# Revit family: E_Cable Tray Support_MEPcontent_OBO Bettermann_Bracket AW FT
name_source: partatom
category: Cable Tray Fittings
revit_build: Autodesk Revit MEP 2015 (Build: 20140606_1530(x64)
units: mm (PartAtom-declared; Revit-internal decimal feet)

## types (34) — shared parameters
Article Description = Wall Bracket
Description = Wall Bracket
EMCS Version = 2.0
ETIM Article Class = EC000022
Family Version = 10.14
Gray = Color RGB 189-187-185
IFCExportAs = IfcCableCarrierFittingType
IFCExportType = NOTDEFINED
MEPcontent Class = CABLE_TRAY_SUPPORT
Manufacturer = OBO BETTERMANN
Manufacturer URL = http://catalog4.obo-bettermann.com
Product Line = OBO BETTERMANN CableTrays
Revit Version = 2015
URL = www.stabiplan.com

## per-type parameters (varying)
| type | Depth | Front Height | GTIN | Height | Height 1 | Manufacturer Art. No. | Width | Width 1 |
| AW 15 11 FT | 40 mm  [stored 0.131234 ft] | 12.5 mm  [stored 0.0410105 ft] | 4012196207077 | 50 mm | 50 mm  [stored 0.164042 ft] | 6420656 | 110 mm | 110 mm  [stored 0.360892 ft] |
| AW 15 16 FT | 40 mm  [stored 0.131234 ft] | 13.75 mm  [stored 0.0451115 ft] | 4012196207138 | 55 mm | 55 mm  [stored 0.180446 ft] | 6420664 | 160 mm | 160 mm  [stored 0.524934 ft] |
| AW 15 21 FT | 40 mm  [stored 0.131234 ft] | 15 mm  [stored 0.0492126 ft] | 4012196207190 | 60 mm | 60 mm  [stored 0.19685 ft] | 6420680 | 210 mm | 210 mm  [stored 0.688976 ft] |
| AW 15 31 FT | 40 mm  [stored 0.131234 ft] | 16.25 mm  [stored 0.0533136 ft] | 4012196207251 | 65 mm | 65 mm  [stored 0.213255 ft] | 6420710 | 310 mm | 310 mm  [stored 1.01706 ft] |
| AW 15 41 FT | 40 mm  [stored 0.131234 ft] | 17.5 mm  [stored 0.0574147 ft] | 4012196207312 | 70 mm | 70 mm  [stored 0.229659 ft] | 6420745 | 410 mm | 410 mm |
| AW 15 51 FT | 40 mm  [stored 0.131234 ft] | 18.75 mm | 4012196207374 | 75 mm | 75 mm | 6420788 | 510 mm | 510 mm |
| AW 15 56 FT | 40 mm  [stored 0.131234 ft] | 20 mm  [stored 0.0656168 ft] | 4012196207435 | 80 mm | 80 mm  [stored 0.262467 ft] | 6420796 | 560 mm | 560 mm |
| AW 15 61 FT | 40 mm  [stored 0.131234 ft] | 20 mm  [stored 0.0656168 ft] | 4012196207497 | 80 mm | 80 mm  [stored 0.262467 ft] | 6420826 | 610 mm | 610 mm |
| AW 30 11 FT | 50 mm  [stored 0.164042 ft] | 15 mm  [stored 0.0492126 ft] | 4012196206599 | 60 mm | 60 mm  [stored 0.19685 ft] | 6419704 | 110 mm | 110 mm  [stored 0.360892 ft] |
| AW 30 16 FT | 50 mm  [stored 0.164042 ft] | 16.25 mm  [stored 0.0533136 ft] | 4012196206650 | 65 mm | 65 mm  [stored 0.213255 ft] | 6419712 | 160 mm | 160 mm  [stored 0.524934 ft] |
| AW 30 21 FT | 50 mm  [stored 0.164042 ft] | 17.5 mm  [stored 0.0574147 ft] | 4012196206711 | 70 mm | 70 mm  [stored 0.229659 ft] | 6419720 | 210 mm | 210 mm  [stored 0.688976 ft] |
| AW 30 31 FT | 50 mm  [stored 0.164042 ft] | 20 mm  [stored 0.0656168 ft] | 4012196206773 | 80 mm | 80 mm  [stored 0.262467 ft] | 6419747 | 310 mm | 310 mm  [stored 1.01706 ft] |
| AW 30 41 FT | 50 mm  [stored 0.164042 ft] | 20 mm  [stored 0.0656168 ft] | 4012196206834 | 80 mm | 80 mm  [stored 0.262467 ft] | 6419763 | 410 mm | 410 mm |
| AW 30 51 FT | 50 mm  [stored 0.164042 ft] | 22.5 mm  [stored 0.0738189 ft] | 4012196206896 | 90 mm | 90 mm  [stored 0.295276 ft] | 6419798 | 510 mm | 510 mm |
| AW 30 56 FT | 50 mm  [stored 0.164042 ft] | 25 mm  [stored 0.082021 ft] | 4012196207015 | 100 mm | 100 mm  [stored 0.328084 ft] | 6419844 | 560 mm | 560 mm |
| AW 30 61 FT | 50 mm  [stored 0.164042 ft] | 25 mm  [stored 0.082021 ft] | 4012196206957 | 100 mm | 100 mm  [stored 0.328084 ft] | 6419828 | 610 mm | 610 mm |
| AW 30 71 FT | 50 mm  [stored 0.164042 ft] | 25 mm  [stored 0.082021 ft] | 4012196483730 | 100 mm | 100 mm  [stored 0.328084 ft] | 6419836 | 710 mm | 710 mm |
| AW 55 21 FT | 50 mm  [stored 0.164042 ft] | 22.5 mm  [stored 0.0738189 ft] | 4012196204731 | 90 mm | 90 mm  [stored 0.295276 ft] | 6418554 | 210 mm | 210 mm  [stored 0.688976 ft] |
| AW 55 31 FT | 50 mm  [stored 0.164042 ft] | 27.5 mm  [stored 0.0902231 ft] | 4012196204793 | 110 mm | 110 mm  [stored 0.360892 ft] | 6418570 | 310 mm | 310 mm  [stored 1.01706 ft] |
| AW 55 41 FT | 50 mm  [stored 0.164042 ft] | 32.5 mm  [stored 0.106627 ft] | 4012196204854 | 130 mm | 130 mm  [stored 0.426509 ft] | 6418597 | 410 mm | 410 mm |
| AW 55 51 FT | 60 mm  [stored 0.19685 ft] | 36.25 mm  [stored 0.11893 ft] | 4012196204915 | 145 mm | 145 mm  [stored 0.475722 ft] | 6418619 | 510 mm | 510 mm |
| AW 55 56 FT | 60 mm  [stored 0.19685 ft] | 41.25 mm | 4012196204977 | 165 mm | 165 mm | 6418627 | 560 mm | 560 mm |
| AW 55 61 FT | 60 mm  [stored 0.19685 ft] | 41.25 mm | 4012196205035 | 165 mm | 165 mm | 6418635 | 610 mm | 610 mm |
| AW 55 71 FT | 60 mm  [stored 0.19685 ft] | 48.75 mm  [stored 0.159941 ft] | 4012196205097 | 195 mm | 195 mm  [stored 0.639764 ft] | 6418651 | 710 mm | 710 mm |
| AW 55 81 FT | 60 mm  [stored 0.19685 ft] | 48.75 mm  [stored 0.159941 ft] | 4012196205158 | 195 mm | 195 mm  [stored 0.639764 ft] | 6418686 | 810 mm | 810 mm |
| AW 55 91 FT | 60 mm  [stored 0.19685 ft] | 53.75 mm | 4012196205219 | 215 mm | 215 mm | 6418708 | 910 mm | 910 mm |
| AW 55 101 FT | 60 mm  [stored 0.19685 ft] | 57.5 mm  [stored 0.188648 ft] | 4012196205271 | 230 mm | 230 mm  [stored 0.754593 ft] | 6418724 | 1010 mm | 1010 mm |
| AW 80 21 FT | 50 mm  [stored 0.164042 ft] | 27.5 mm  [stored 0.0902231 ft] | 4012196203475 | 110 mm | 110 mm  [stored 0.360892 ft] | 6417752 | 210 mm | 210 mm  [stored 0.688976 ft] |
| AW 80 31 FT | 50 mm  [stored 0.164042 ft] | 36.25 mm  [stored 0.11893 ft] | 4012196203536 | 145 mm | 145 mm  [stored 0.475722 ft] | 6417779 | 310 mm | 310 mm  [stored 1.01706 ft] |
| AW 80 41 FT | 50 mm  [stored 0.164042 ft] | 41.25 mm | 4012196203598 | 165 mm | 165 mm | 6417795 | 410 mm | 410 mm |
| AW 80 51 FT | 60 mm  [stored 0.19685 ft] | 48.75 mm  [stored 0.159941 ft] | 4012196203659 | 195 mm | 195 mm  [stored 0.639764 ft] | 6417817 | 510 mm | 510 mm |
| AW 80 61 FT | 60 mm  [stored 0.19685 ft] | 52.5 mm  [stored 0.172244 ft] | 4012196203710 | 210 mm | 210 mm  [stored 0.688976 ft] | 6417833 | 610 mm | 610 mm |
| AW 80 71 FT | 60 mm  [stored 0.19685 ft] | 58.75 mm  [stored 0.192749 ft] | 4012196203772 | 235 mm | 235 mm  [stored 0.770997 ft] | 6417868 | 710 mm | 710 mm |
| AW 80 81 FT | 60 mm  [stored 0.19685 ft] | 65 mm  [stored 0.213255 ft] | 4012196203833 | 260 mm | 260 mm  [stored 0.853018 ft] | 6417884 | 810 mm | 810 mm |

note: column(s) folded — value = type name in every type: Article Type, Model

note: [stored X ft] marks values corroborated as IEEE doubles in the binary element streams (Revit-internal decimal feet)

## geometry (parser evidence)
native form markers: Blend x4, Sweep x3
no freeform markers — native parametric forms only
